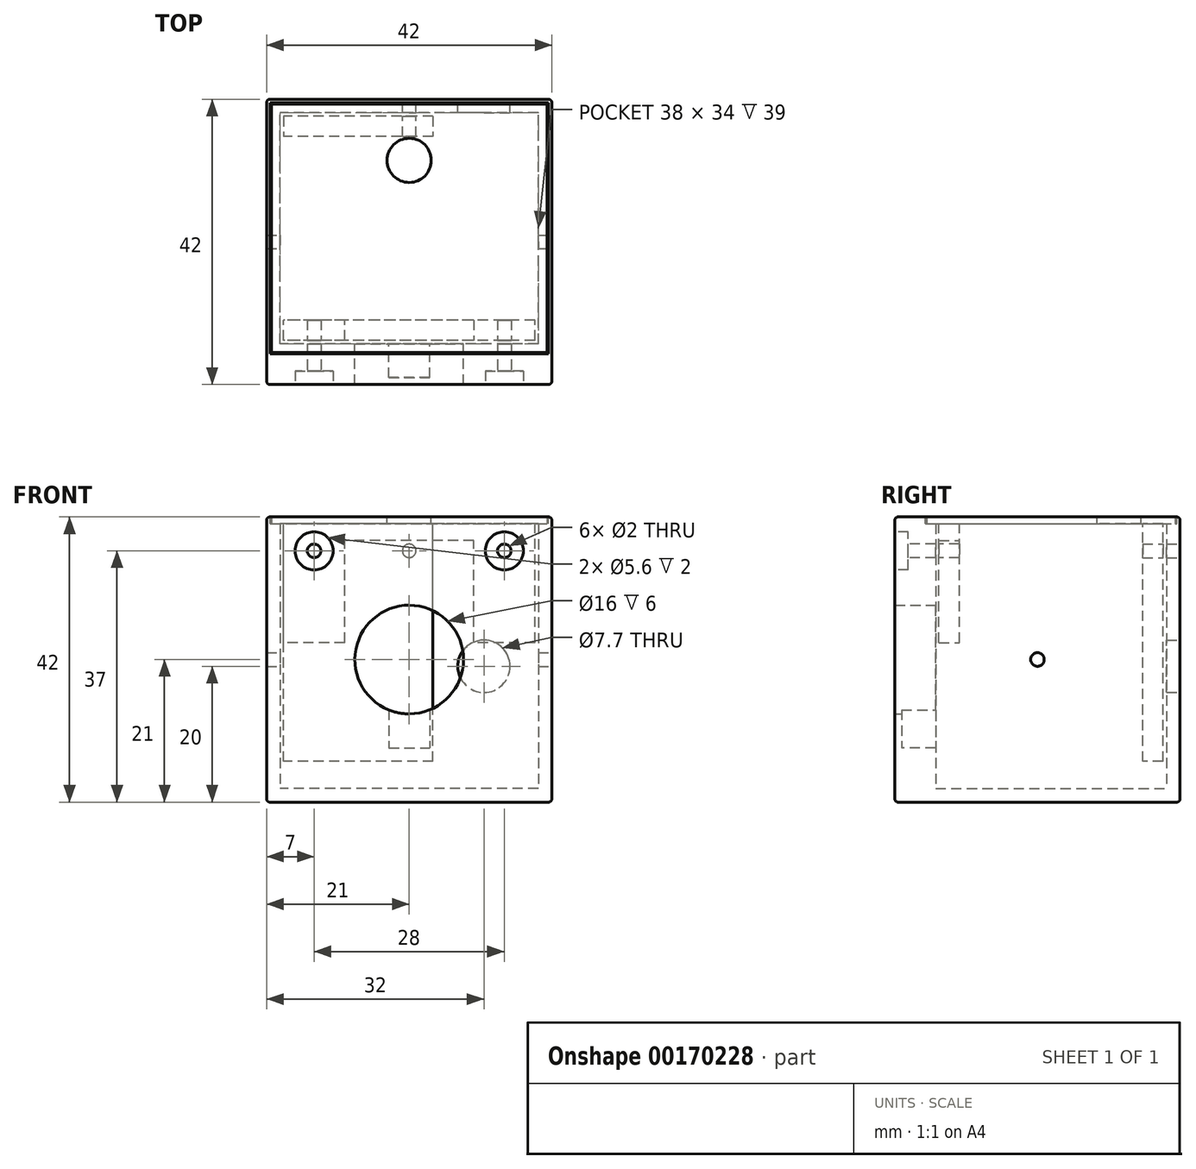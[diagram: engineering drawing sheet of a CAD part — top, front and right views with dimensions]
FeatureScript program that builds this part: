
annotation { "Feature Type Name" : "Feature", "Feature Type Description" : "" }
export const myFeature = defineFeature(function(context is Context, id is Id, definition is map)
    precondition{}
    {
        {
            var Q0;
            Q0=qCreatedBy(makeId("Top.planeOp"),FACE);
            var sketch = newSketch(context, id + "F0", { "sketchPlane" : qUnion([Q0])});
            skLineSegment(sketch, "E0.bottom", {"start": v(21, -21) * mm, "end": v(-21, -21) * mm});
            skLineSegment(sketch, "E0.top", {"start": v(21, 21) * mm, "end": v(-21, 21) * mm});
            skLineSegment(sketch, "E0.left", {"start": v(21, -21) * mm, "end": v(21, 21) * mm});
            skLineSegment(sketch, "E0.right", {"start": v(-21, -21) * mm, "end": v(-21, 21) * mm});
            skPoint(sketch, "E0.middle", {"position": v(0, 0) * mm});
            skSolve(sketch);
        }
        {
            var Q0;
            Q0 = qSketchRegion(id + "F0", true);
            extrude(context, id + "F1", {"entities" : qUnion([Q0]), "depth" : 42 * mm});
        }
        {
            var Q0;
            Q0=makeQuery(id+"F1.opExtrude","CAP_FACE",FACE,{"disambiguationData":[OSD([sQuery(id+"F0.wireOp",EDGE,"E0.bottom"),sQuery(id+"F0.wireOp",EDGE,"E0.top"),sQuery(id+"F0.wireOp",EDGE,"E0.left"),sQuery(id+"F0.wireOp",EDGE,"E0.right")])],"isStart":false});
            shell(context, id + "F2", {"entities" : qUnion([Q0]), "thickness" : 2 * mm});
        }
        {
            var Q0;
            Q0=qCreatedBy(makeId("Front.planeOp"),FACE);
            var sketch = newSketch(context, id + "F3", { "sketchPlane" : qUnion([Q0])});
            skCircle(sketch, "E1", {"center": v(0, 21) * mm, "radius": 8 * mm});
            skSolve(sketch);
        }
        {
            var Q0;
            Q0 = qSketchRegion(id + "F3", true);
            extrude(context, id + "F4", {"entities" : qUnion([Q0]), "operationType" : NewBodyOperationType.REMOVE, "endBound" : BoundingType.THROUGH_ALL, "depth" : 25 * mm});
        }
        {
            var Q0;
            Q0=makeQuery(id+"F2.opShell","OFFSET_FACE",FACE,{"disambiguationData":[OSD([sQuery(id+"F0.wireOp",EDGE,"E0.bottom")])]});
            extrude(context, id + "F5", {"entities" : qUnion([Q0]), "operationType" : NewBodyOperationType.ADD, "depth" : 4 * mm});
        }
        {
            var Q0;
            Q0=qCreatedBy(makeId("Top.planeOp"),FACE);
            cPlane(context, id + "F6", {"entities" : qUnion([Q0]), "cplaneType" : CPlaneType.OFFSET, "offset" : 8 * mm, "width" : 150 * mm, "height" : 150 * mm});
        }
        {
            var Q0;
            Q0=qCreatedBy(id+"F6.planeOp",FACE);
            var sketch = newSketch(context, id + "F7", { "sketchPlane" : qUnion([Q0])});
            skLineSegment(sketch, "E2.bottom", {"start": v(-3, -15) * mm, "end": v(3, -15) * mm});
            skLineSegment(sketch, "E2.top", {"start": v(-3, -20) * mm, "end": v(3, -20) * mm});
            skLineSegment(sketch, "E2.left", {"start": v(-3, -15) * mm, "end": v(-3, -20) * mm});
            skLineSegment(sketch, "E2.right", {"start": v(3, -15) * mm, "end": v(3, -20) * mm});
            skSolve(sketch);
        }
        {
            var Q0;
            Q0 = qSketchRegion(id + "F7", true);
            extrude(context, id + "F8", {"entities" : qUnion([Q0]), "operationType" : NewBodyOperationType.REMOVE, "endBound" : BoundingType.UP_TO_NEXT, "depth" : 25 * mm});
        }
        {
            var Q0;
            Q0=makeQuery(id+"F1.opExtrude","SWEPT_FACE",FACE,{"disambiguationData":[OSD([sQuery(id+"F0.wireOp",EDGE,"E0.top")])]});
            var sketch = newSketch(context, id + "F9", { "sketchPlane" : qUnion([Q0])});
            skCircle(sketch, "E3", {"center": v(-11, 20) * mm, "radius": 3.85 * mm});
            skSolve(sketch);
        }
        {
            var Q0;
            Q0 = qSketchRegion(id + "F9", true);
            extrude(context, id + "F10", {"entities" : qUnion([Q0]), "operationType" : NewBodyOperationType.REMOVE, "endBound" : BoundingType.UP_TO_NEXT, "oppositeDirection" : true, "depth" : 25 * mm});
        }
        {
            var Q0;
            {var subQ0=sQuery(id+"F0.wireOp",EDGE,"E0.bottom");Q0=makeQuery(id+"F5.boolean.opBoolean","MERGE",FACE,{"derivedFrom":[makeQuery(id+"F1.opExtrude","CAP_FACE",FACE,{"disambiguationData":[OSD([subQ0,sQuery(id+"F0.wireOp",EDGE,"E0.top"),sQuery(id+"F0.wireOp",EDGE,"E0.left"),sQuery(id+"F0.wireOp",EDGE,"E0.right")])],"isStart":false}),makeQuery(id+"F5.opExtrude","SWEPT_FACE",FACE,{"disambiguationData":[OSD([subQ0]),TDD([makeQuery(id+"F2.opShell","OFFSET_EDGE",EDGE,{"disambiguationData":[OSD([subQ0]),TDD([makeQuery(id+"F1.opExtrude","CAP_EDGE",EDGE,{"disambiguationData":[OSD([subQ0])],"isStart":false})])]})])]})]});}
            var sketch = newSketch(context, id + "F11", { "sketchPlane" : qUnion([Q0])});
            skLineSegment(sketch, "E4.bottom", {"start": v(-20.5, -16.5) * mm, "end": v(20.5, -16.5) * mm});
            skLineSegment(sketch, "E4.top", {"start": v(-20.5, 20.5) * mm, "end": v(20.5, 20.5) * mm});
            skLineSegment(sketch, "E4.left", {"start": v(-20.5, -16.5) * mm, "end": v(-20.5, 20.5) * mm});
            skLineSegment(sketch, "E4.right", {"start": v(20.5, -16.5) * mm, "end": v(20.5, 20.5) * mm});
            skSolve(sketch);
        }
        {
            var Q0;
            Q0 = qSketchRegion(id + "F11", true);
            extrude(context, id + "F12", {"entities" : qUnion([Q0]), "operationType" : NewBodyOperationType.REMOVE, "oppositeDirection" : true, "depth" : 1 * mm});
        }
        {
            var Q0;
            Q0=makeQuery(id+"F12.boolean.opBoolean","COPY",FACE,{"derivedFrom":makeQuery(id+"F12.opExtrude","CAP_FACE",FACE,{"disambiguationData":[OSD([sQuery(id+"F11.wireOp",EDGE,"E4.bottom"),sQuery(id+"F11.wireOp",EDGE,"E4.top"),sQuery(id+"F11.wireOp",EDGE,"E4.left"),sQuery(id+"F11.wireOp",EDGE,"E4.right")])],"isStart":false})});
            var sketch = newSketch(context, id + "F13", { "sketchPlane" : qUnion([Q0])});
            skLineSegment(sketch, "E5.bottom", {"start": v(-20.3, -16.3) * mm, "end": v(20.3, -16.3) * mm});
            skLineSegment(sketch, "E5.top", {"start": v(-20.3, 20.3) * mm, "end": v(20.3, 20.3) * mm});
            skLineSegment(sketch, "E5.left", {"start": v(-20.3, -16.3) * mm, "end": v(-20.3, 20.3) * mm});
            skLineSegment(sketch, "E5.right", {"start": v(20.3, -16.3) * mm, "end": v(20.3, 20.3) * mm});
            skSolve(sketch);
        }
        {
            var Q0;
            Q0 = qSketchRegion(id + "F13", true);
            var Q1;
            {var subQ0=sQuery(id+"F0.wireOp",EDGE,"E0.bottom");Q1=makeQuery(id+"F5.boolean.opBoolean","MERGE",FACE,{"derivedFrom":[makeQuery(id+"F1.opExtrude","CAP_FACE",FACE,{"disambiguationData":[OSD([subQ0,sQuery(id+"F0.wireOp",EDGE,"E0.top"),sQuery(id+"F0.wireOp",EDGE,"E0.left"),sQuery(id+"F0.wireOp",EDGE,"E0.right")])],"isStart":false}),makeQuery(id+"F5.opExtrude","SWEPT_FACE",FACE,{"disambiguationData":[OSD([subQ0]),TDD([makeQuery(id+"F2.opShell","OFFSET_EDGE",EDGE,{"disambiguationData":[OSD([subQ0]),TDD([makeQuery(id+"F1.opExtrude","CAP_EDGE",EDGE,{"disambiguationData":[OSD([subQ0])],"isStart":false})])]})])]})]});}
            extrude(context, id + "F14", {"entities" : qUnion([Q0]), "endBound" : BoundingType.UP_TO_SURFACE, "endBoundEntityFace" : qUnion([Q1]), "depth" : 25 * mm});
        }
        {
            var Q0;
            Q0=makeQuery(id+"F14.opExtrude","CAP_FACE",FACE,{"disambiguationData":[OSD([sQuery(id+"F13.wireOp",EDGE,"E5.bottom"),sQuery(id+"F13.wireOp",EDGE,"E5.top"),sQuery(id+"F13.wireOp",EDGE,"E5.left"),sQuery(id+"F13.wireOp",EDGE,"E5.right")])],"isStart":true});
            var sketch = newSketch(context, id + "F15", { "sketchPlane" : qUnion([Q0])});
            skLineSegment(sketch, "E6.bottom", {"start": v(3.5, -18.5) * mm, "end": v(-18.5, -18.5) * mm});
            skLineSegment(sketch, "E6.top", {"start": v(3.5, -15.5) * mm, "end": v(-18.5, -15.5) * mm});
            skLineSegment(sketch, "E6.left", {"start": v(3.5, -18.5) * mm, "end": v(3.5, -15.5) * mm});
            skLineSegment(sketch, "E6.right", {"start": v(-18.5, -18.5) * mm, "end": v(-18.5, -15.5) * mm});
            skSolve(sketch);
        }
        {
            var Q0;
            Q0 = qSketchRegion(id + "F15", true);
            extrude(context, id + "F16", {"entities" : qUnion([Q0]), "operationType" : NewBodyOperationType.ADD, "depth" : 35 * mm});
        }
        {
            var Q0;
            Q0=makeQuery(id+"F14.opExtrude","CAP_FACE",FACE,{"disambiguationData":[OSD([sQuery(id+"F13.wireOp",EDGE,"E5.bottom"),sQuery(id+"F13.wireOp",EDGE,"E5.top"),sQuery(id+"F13.wireOp",EDGE,"E5.left"),sQuery(id+"F13.wireOp",EDGE,"E5.right")])],"isStart":true});
            var sketch = newSketch(context, id + "F17", { "sketchPlane" : qUnion([Q0])});
            skLineSegment(sketch, "E7.bottom", {"start": v(18.5, 14.5) * mm, "end": v(-18.5, 14.5) * mm});
            skLineSegment(sketch, "E7.top", {"start": v(18.5, 11.5) * mm, "end": v(-18.5, 11.5) * mm});
            skLineSegment(sketch, "E7.left", {"start": v(18.5, 14.5) * mm, "end": v(18.5, 11.5) * mm});
            skLineSegment(sketch, "E7.right", {"start": v(-18.5, 14.5) * mm, "end": v(-18.5, 11.5) * mm});
            skSolve(sketch);
        }
        {
            var Q0;
            Q0 = qSketchRegion(id + "F17", true);
            extrude(context, id + "F18", {"entities" : qUnion([Q0]), "operationType" : NewBodyOperationType.ADD, "depth" : 2.5 * mm});
        }
        {
            var Q0;
            Q0=makeQuery(id+"F18.opExtrude","CAP_FACE",FACE,{"disambiguationData":[OSD([sQuery(id+"F17.wireOp",EDGE,"E7.bottom"),sQuery(id+"F17.wireOp",EDGE,"E7.top"),sQuery(id+"F17.wireOp",EDGE,"E7.left"),sQuery(id+"F17.wireOp",EDGE,"E7.right")])],"isStart":false});
            var sketch = newSketch(context, id + "F19", { "sketchPlane" : qUnion([Q0])});
            skLineSegment(sketch, "E8.bottom", {"start": v(18.5, 11.5) * mm, "end": v(9.5, 11.5) * mm});
            skLineSegment(sketch, "E8.top", {"start": v(18.5, 14.5) * mm, "end": v(9.5, 14.5) * mm});
            skLineSegment(sketch, "E8.left", {"start": v(18.5, 11.5) * mm, "end": v(18.5, 14.5) * mm});
            skLineSegment(sketch, "E8.right", {"start": v(9.5, 11.5) * mm, "end": v(9.5, 14.5) * mm});
            skLineSegment(sketch, "E9.bottom", {"start": v(-18.5, 14.5) * mm, "end": v(-9.5, 14.5) * mm});
            skLineSegment(sketch, "E9.top", {"start": v(-18.5, 11.5) * mm, "end": v(-9.5, 11.5) * mm});
            skLineSegment(sketch, "E9.left", {"start": v(-18.5, 14.5) * mm, "end": v(-18.5, 11.5) * mm});
            skLineSegment(sketch, "E9.right", {"start": v(-9.5, 14.5) * mm, "end": v(-9.5, 11.5) * mm});
            skSolve(sketch);
        }
        {
            var Q0;
            Q0 = qSketchRegion(id + "F19", true);
            extrude(context, id + "F20", {"entities" : qUnion([Q0]), "operationType" : NewBodyOperationType.ADD, "depth" : 15 * mm});
        }
        {
            var Q0;
            Q0=makeQuery(id+"F1.opExtrude","SWEPT_FACE",FACE,{"disambiguationData":[OSD([sQuery(id+"F0.wireOp",EDGE,"E0.top")])]});
            var sketch = newSketch(context, id + "F21", { "sketchPlane" : qUnion([Q0])});
            skCircle(sketch, "E10", {"center": v(0, 37) * mm, "radius": 1 * mm});
            skSolve(sketch);
        }
        {
            var Q0;
            Q0 = qSketchRegion(id + "F21", true);
            extrude(context, id + "F22", {"entities" : qUnion([Q0]), "operationType" : NewBodyOperationType.REMOVE, "oppositeDirection" : true, "depth" : 10 * mm});
        }
        {
            var Q0;
            Q0=makeQuery(id+"F1.opExtrude","SWEPT_FACE",FACE,{"disambiguationData":[OSD([sQuery(id+"F0.wireOp",EDGE,"E0.bottom")])]});
            var sketch = newSketch(context, id + "F23", { "sketchPlane" : qUnion([Q0])});
            skCircle(sketch, "E11", {"center": v(-14, 37) * mm, "radius": 1 * mm});
            skCircle(sketch, "E12", {"center": v(14, 37) * mm, "radius": 1 * mm});
            skSolve(sketch);
        }
        {
            var Q0;
            Q0 = qSketchRegion(id + "F23", true);
            extrude(context, id + "F24", {"entities" : qUnion([Q0]), "operationType" : NewBodyOperationType.REMOVE, "oppositeDirection" : true, "depth" : 25 * mm});
        }
        {
            var Q0;
            Q0=makeQuery(id+"F1.opExtrude","SWEPT_FACE",FACE,{"disambiguationData":[OSD([sQuery(id+"F0.wireOp",EDGE,"E0.bottom")])]});
            var sketch = newSketch(context, id + "F25", { "sketchPlane" : qUnion([Q0])});
            skCircle(sketch, "E13", {"center": v(14, 37) * mm, "radius": 2.8 * mm});
            skCircle(sketch, "E14", {"center": v(-14, 37) * mm, "radius": 2.8 * mm});
            skSolve(sketch);
        }
        {
            var Q0;
            Q0 = qSketchRegion(id + "F25", true);
            extrude(context, id + "F26", {"entities" : qUnion([Q0]), "operationType" : NewBodyOperationType.REMOVE, "oppositeDirection" : true, "depth" : 2 * mm});
        }
        {
            var Q0;
            Q0=makeQuery(id+"F1.opExtrude","SWEPT_FACE",FACE,{"disambiguationData":[OSD([sQuery(id+"F0.wireOp",EDGE,"E0.left")])]});
            var sketch = newSketch(context, id + "F27", { "sketchPlane" : qUnion([Q0])});
            skLineSegment(sketch, "E15", {"start": v(-21, 42) * mm, "end": v(21, 0) * mm, "construction": true});
            skLineSegment(sketch, "E16", {"start": v(21, 42) * mm, "end": v(-21, 0) * mm, "construction": true});
            skCircle(sketch, "E17", {"center": v(0, 21) * mm, "radius": 1 * mm});
            skSolve(sketch);
        }
        {
            var Q0;
            Q0 = qSketchRegion(id + "F27", true);
            extrude(context, id + "F28", {"entities" : qUnion([Q0]), "operationType" : NewBodyOperationType.REMOVE, "endBound" : BoundingType.THROUGH_ALL, "oppositeDirection" : true, "depth" : 25 * mm});
        }
        {
            var Q0;
            Q0=makeQuery(id+"F14.opExtrude","CAP_FACE",FACE,{"disambiguationData":[OSD([sQuery(id+"F13.wireOp",EDGE,"E5.bottom"),sQuery(id+"F13.wireOp",EDGE,"E5.top"),sQuery(id+"F13.wireOp",EDGE,"E5.left"),sQuery(id+"F13.wireOp",EDGE,"E5.right")])],"isStart":false});
            var sketch = newSketch(context, id + "F29", { "sketchPlane" : qUnion([Q0])});
            skCircle(sketch, "E18", {"center": v(0, 12) * mm, "radius": 3.25 * mm});
            skSolve(sketch);
        }
        {
            var Q0;
            Q0 = qSketchRegion(id + "F29", true);
            extrude(context, id + "F30", {"entities" : qUnion([Q0]), "operationType" : NewBodyOperationType.REMOVE, "endBound" : BoundingType.UP_TO_NEXT, "oppositeDirection" : true, "depth" : 25 * mm});
        }
        {
            var Q0;
            Q0=makeQuery(id+"F1.opExtrude","CAP_EDGE",EDGE,{"disambiguationData":[OSD([sQuery(id+"F0.wireOp",EDGE,"E0.left")])],"isStart":false});
            var Q1;
            Q1=makeQuery(id+"F1.opExtrude","CAP_EDGE",EDGE,{"disambiguationData":[OSD([sQuery(id+"F0.wireOp",EDGE,"E0.top")])],"isStart":false});
            var Q2;
            Q2=makeQuery(id+"F1.opExtrude","SWEPT_EDGE",EDGE,{"disambiguationData":[OSD([sQuery(id+"F0.wireOp",EDGE,"E0.top"),sQuery(id+"F0.wireOp",EDGE,"E0.left")])]});
            var Q3;
            Q3=makeQuery(id+"F1.opExtrude","SWEPT_EDGE",EDGE,{"disambiguationData":[OSD([sQuery(id+"F0.wireOp",EDGE,"E0.top"),sQuery(id+"F0.wireOp",EDGE,"E0.right")])]});
            var Q4;
            Q4=makeQuery(id+"F1.opExtrude","CAP_EDGE",EDGE,{"disambiguationData":[OSD([sQuery(id+"F0.wireOp",EDGE,"E0.top")])],"isStart":true});
            var Q5;
            Q5=makeQuery(id+"F1.opExtrude","CAP_EDGE",EDGE,{"disambiguationData":[OSD([sQuery(id+"F0.wireOp",EDGE,"E0.left")])],"isStart":true});
            var Q6;
            Q6=makeQuery(id+"F1.opExtrude","SWEPT_EDGE",EDGE,{"disambiguationData":[OSD([sQuery(id+"F0.wireOp",EDGE,"E0.bottom"),sQuery(id+"F0.wireOp",EDGE,"E0.left")])]});
            var Q7;
            Q7=makeQuery(id+"F1.opExtrude","CAP_EDGE",EDGE,{"disambiguationData":[OSD([sQuery(id+"F0.wireOp",EDGE,"E0.bottom")])],"isStart":false});
            var Q8;
            Q8=makeQuery(id+"F1.opExtrude","CAP_EDGE",EDGE,{"disambiguationData":[OSD([sQuery(id+"F0.wireOp",EDGE,"E0.right")])],"isStart":false});
            var Q9;
            Q9=makeQuery(id+"F1.opExtrude","SWEPT_EDGE",EDGE,{"disambiguationData":[OSD([sQuery(id+"F0.wireOp",EDGE,"E0.bottom"),sQuery(id+"F0.wireOp",EDGE,"E0.right")])]});
            var Q10;
            Q10=makeQuery(id+"F1.opExtrude","CAP_EDGE",EDGE,{"disambiguationData":[OSD([sQuery(id+"F0.wireOp",EDGE,"E0.right")])],"isStart":true});
            var Q11;
            Q11=makeQuery(id+"F1.opExtrude","CAP_EDGE",EDGE,{"disambiguationData":[OSD([sQuery(id+"F0.wireOp",EDGE,"E0.bottom")])],"isStart":true});
            fillet(context, id + "F31", {"entities" : qUnion([Q0, Q1, Q2, Q3, Q4, Q5, Q6, Q7, Q8, Q9, Q10, Q11]), "radius" : 0.5 * mm, "tangentPropagation" : true, "allowEdgeOverflow" : false});
        }
    });
